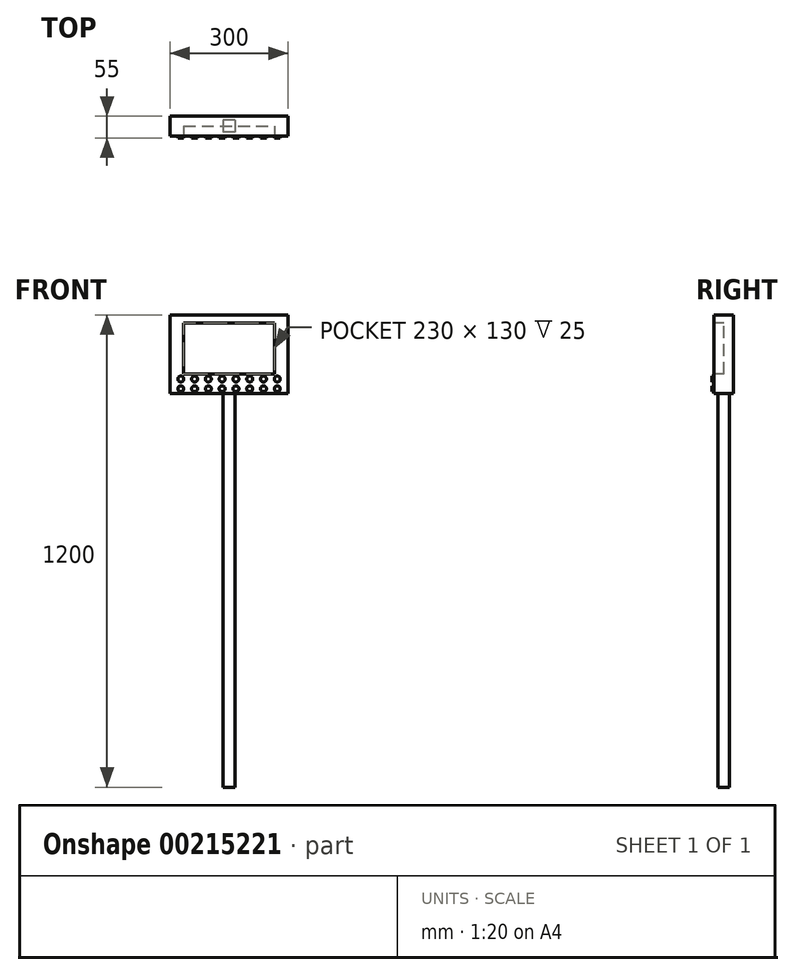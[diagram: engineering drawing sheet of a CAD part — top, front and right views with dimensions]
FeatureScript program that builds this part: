
annotation { "Feature Type Name" : "Feature", "Feature Type Description" : "" }
export const myFeature = defineFeature(function(context is Context, id is Id, definition is map)
    precondition{}
    {
        {
            var Q0;
            Q0=qCreatedBy(makeId("Front.planeOp"),FACE);
            var sketch = newSketch(context, id + "F0", { "sketchPlane" : qUnion([Q0])});
            skLineSegment(sketch, "E0.bottom", {"start": v(150, -100) * mm, "end": v(-150, -100) * mm});
            skLineSegment(sketch, "E0.top", {"start": v(150, 100) * mm, "end": v(-150, 100) * mm});
            skLineSegment(sketch, "E0.left", {"start": v(150, -100) * mm, "end": v(150, 100) * mm});
            skLineSegment(sketch, "E0.right", {"start": v(-150, -100) * mm, "end": v(-150, 100) * mm});
            skPoint(sketch, "E0.middle", {"position": v(0, 0) * mm});
            skSolve(sketch);
        }
        {
            var Q0;
            Q0 = qSketchRegion(id + "F0", true);
            extrude(context, id + "F1", {"entities" : qUnion([Q0]), "oppositeDirection" : true, "depth" : 50 * mm});
        }
        {
            var Q0;
            Q0=makeQuery(id+"F1.opExtrude","CAP_FACE",FACE,{"disambiguationData":[OSD([sQuery(id+"F0.wireOp",EDGE,"E0.bottom"),sQuery(id+"F0.wireOp",EDGE,"E0.top"),sQuery(id+"F0.wireOp",EDGE,"E0.left"),sQuery(id+"F0.wireOp",EDGE,"E0.right")])],"isStart":true});
            var sketch = newSketch(context, id + "F2", { "sketchPlane" : qUnion([Q0])});
            skLineSegment(sketch, "E1.bottom", {"start": v(-115, -50) * mm, "end": v(115, -50) * mm});
            skLineSegment(sketch, "E1.top", {"start": v(-115, 80) * mm, "end": v(115, 80) * mm});
            skLineSegment(sketch, "E1.left", {"start": v(-115, -50) * mm, "end": v(-115, 80) * mm});
            skLineSegment(sketch, "E1.right", {"start": v(115, -50) * mm, "end": v(115, 80) * mm});
            skSolve(sketch);
        }
        {
            var Q0;
            Q0 = qSketchRegion(id + "F2", true);
            extrude(context, id + "F3", {"entities" : qUnion([Q0]), "operationType" : NewBodyOperationType.REMOVE, "oppositeDirection" : true, "depth" : 25 * mm});
        }
        {
            var Q0;
            Q0=makeQuery(id+"F3.boolean.opBoolean","COPY",FACE,{"derivedFrom":makeQuery(id+"F3.opExtrude","CAP_FACE",FACE,{"disambiguationData":[OSD([sQuery(id+"F2.wireOp",EDGE,"E1.bottom"),sQuery(id+"F2.wireOp",EDGE,"E1.top"),sQuery(id+"F2.wireOp",EDGE,"E1.left"),sQuery(id+"F2.wireOp",EDGE,"E1.right")])],"isStart":false})});
            var sketch = newSketch(context, id + "F4", { "sketchPlane" : qUnion([Q0])});
            skLineSegment(sketch, "E2.0", {"start": v(-115, 80) * mm, "end": v(115, 80) * mm});
            skLineSegment(sketch, "E3.0", {"start": v(-115, -50) * mm, "end": v(-115, 80) * mm});
            skLineSegment(sketch, "E4.0", {"start": v(-115, -50) * mm, "end": v(115, -50) * mm});
            skLineSegment(sketch, "E5.0", {"start": v(115, -50) * mm, "end": v(115, 80) * mm});
            skSolve(sketch);
        }
        {
            var Q0;
            Q0 = qSketchRegion(id + "F4", true);
            extrude(context, id + "F5", {"entities" : qUnion([Q0]), "depth" : 25 * mm});
        }
        {
            var Q0;
            Q0=makeQuery(id+"F1.opExtrude","CAP_FACE",FACE,{"disambiguationData":[OSD([sQuery(id+"F0.wireOp",EDGE,"E0.bottom"),sQuery(id+"F0.wireOp",EDGE,"E0.top"),sQuery(id+"F0.wireOp",EDGE,"E0.left"),sQuery(id+"F0.wireOp",EDGE,"E0.right")])],"isStart":true});
            var sketch = newSketch(context, id + "F6", { "sketchPlane" : qUnion([Q0])});
            skCircle(sketch, "E6", {"center": v(-122.5, -62.67) * mm, "radius": 7.5 * mm});
            skCircle(sketch, "E7", {"center": v(-122.5, -87.47) * mm, "radius": 7.5 * mm});
            skCircle(sketch, "E8.1.0.0", {"center": v(-87.5, -62.67) * mm, "radius": 7.5 * mm});
            skCircle(sketch, "E8.1.0.1", {"center": v(-87.5, -87.47) * mm, "radius": 7.5 * mm});
            skCircle(sketch, "E8.2.0.0", {"center": v(-52.5, -62.67) * mm, "radius": 7.5 * mm});
            skCircle(sketch, "E8.2.0.1", {"center": v(-52.5, -87.47) * mm, "radius": 7.5 * mm});
            skCircle(sketch, "E8.3.0.0", {"center": v(-17.5, -62.67) * mm, "radius": 7.5 * mm});
            skCircle(sketch, "E8.3.0.1", {"center": v(-17.5, -87.47) * mm, "radius": 7.5 * mm});
            skCircle(sketch, "E8.4.0.0", {"center": v(17.5, -62.67) * mm, "radius": 7.5 * mm});
            skCircle(sketch, "E8.4.0.1", {"center": v(17.5, -87.47) * mm, "radius": 7.5 * mm});
            skCircle(sketch, "E8.5.0.0", {"center": v(52.5, -62.67) * mm, "radius": 7.5 * mm});
            skCircle(sketch, "E8.5.0.1", {"center": v(52.5, -87.47) * mm, "radius": 7.5 * mm});
            skCircle(sketch, "E8.6.0.0", {"center": v(87.5, -62.67) * mm, "radius": 7.5 * mm});
            skCircle(sketch, "E8.6.0.1", {"center": v(87.5, -87.47) * mm, "radius": 7.5 * mm});
            skCircle(sketch, "E8.7.0.0", {"center": v(122.5, -62.67) * mm, "radius": 7.5 * mm});
            skCircle(sketch, "E8.7.0.1", {"center": v(122.5, -87.47) * mm, "radius": 7.5 * mm});
            skLineSegment(sketch, "E8.direction1", {"start": v(-122.5, -62.67) * mm, "end": v(-87.5, -62.67) * mm, "construction": true});
            skSolve(sketch);
        }
        {
            var Q0;
            Q0 = qSketchRegion(id + "F6", true);
            extrude(context, id + "F7", {"entities" : qUnion([Q0]), "depth" : 5 * mm});
        }
        {
            var Q0;
            Q0=makeQuery(id+"F1.opExtrude","SWEPT_FACE",FACE,{"disambiguationData":[OSD([sQuery(id+"F0.wireOp",EDGE,"E0.bottom")])]});
            var sketch = newSketch(context, id + "F8", { "sketchPlane" : qUnion([Q0])});
            skLineSegment(sketch, "E9.bottom", {"start": v(15, -40) * mm, "end": v(-15, -40) * mm});
            skLineSegment(sketch, "E9.top", {"start": v(15, -10) * mm, "end": v(-15, -10) * mm});
            skLineSegment(sketch, "E9.left", {"start": v(15, -40) * mm, "end": v(15, -10) * mm});
            skLineSegment(sketch, "E9.right", {"start": v(-15, -40) * mm, "end": v(-15, -10) * mm});
            skPoint(sketch, "E9.middle", {"position": v(0, -25) * mm});
            skPoint(sketch, "E9.middle.positionSnap0", {"position": v(-150, -25) * mm});
            skPoint(sketch, "E9.middle.positionSnap1", {"position": v(0, -50) * mm});
            skPoint(sketch, "E9.centerSnap0", {"position": v(-150, -25) * mm});
            skPoint(sketch, "E9.centerSnap1", {"position": v(0, -50) * mm});
            skSolve(sketch);
        }
        {
            var Q0;
            Q0 = qSketchRegion(id + "F8", true);
            extrude(context, id + "F9", {"entities" : qUnion([Q0]), "operationType" : NewBodyOperationType.ADD, "depth" : 1000 * mm});
        }
    });
